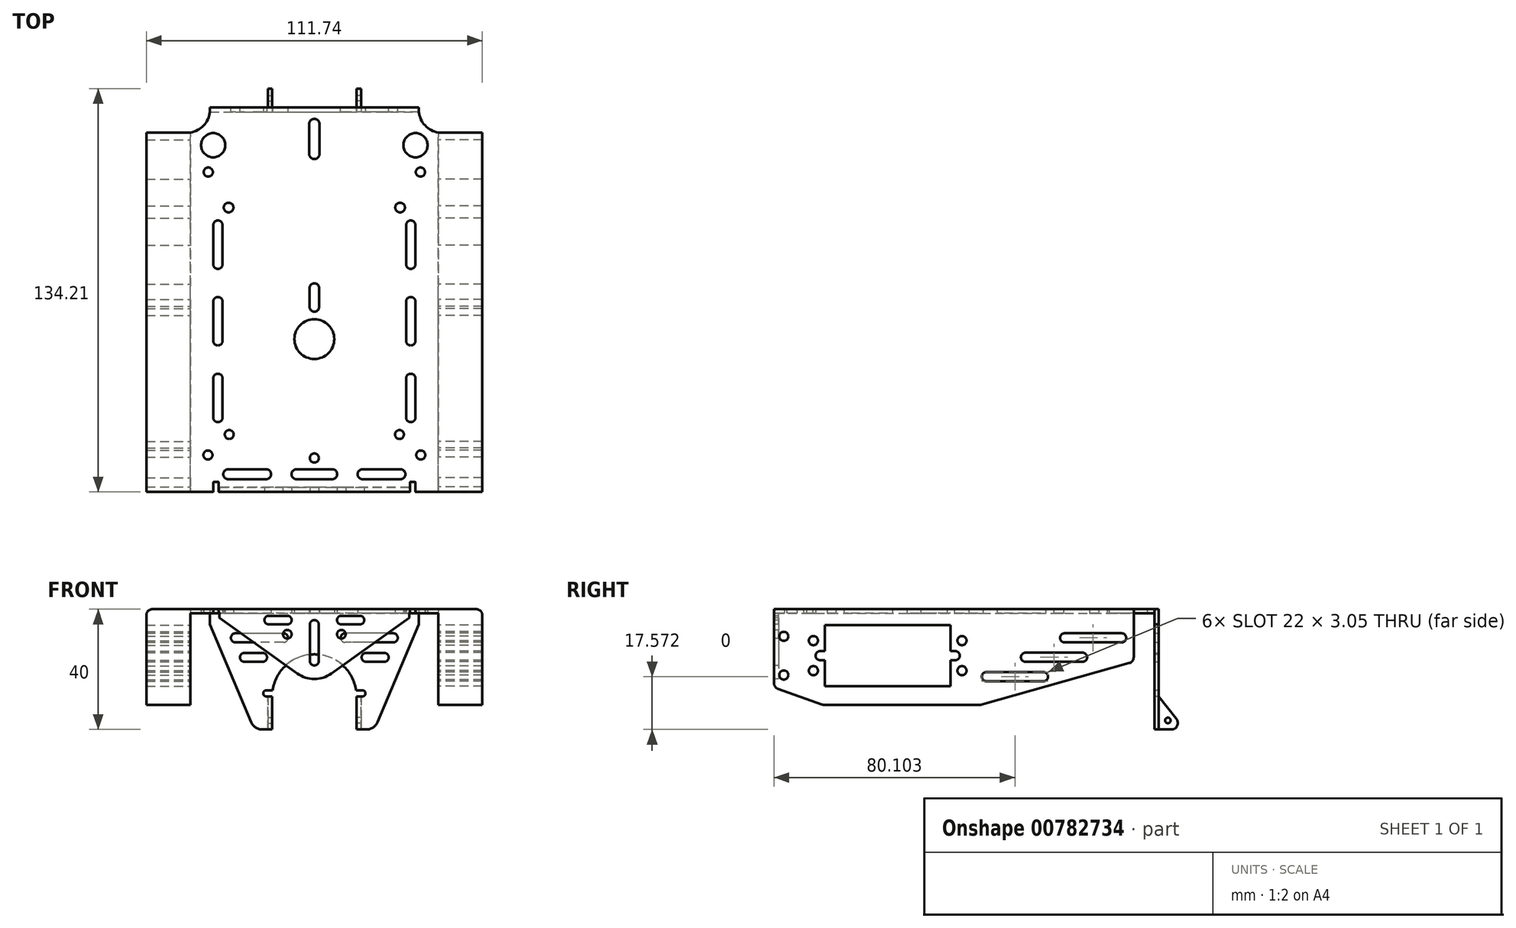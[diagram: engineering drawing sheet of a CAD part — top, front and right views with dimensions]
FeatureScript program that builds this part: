
annotation { "Feature Type Name" : "Feature", "Feature Type Description" : "" }
export const myFeature = defineFeature(function(context is Context, id is Id, definition is map)
    precondition{}
    {
        {
            var Q0;
            Q0=qCreatedBy(makeId("Top.planeOp"),FACE);
            var sketch = newSketch(context, id + "F0", { "sketchPlane" : qUnion([Q0])});
            skLineSegment(sketch, "E0", {"start": v(40.6, 10) * mm, "end": v(40.6, 161.38) * mm});
            skArc(sketch, "E1", {"start": v(40.6, 161.38) * mm, "mid": v(46.2, 164.32) * mm, "end": v(48.85, 170.09) * mm});
            skLineSegment(sketch, "E2", {"start": v(48.85, 170.09) * mm, "end": v(92.83, 170.09) * mm});
            skLineSegment(sketch, "E3", {"start": v(92.83, 170.09) * mm, "end": v(92.83, 10) * mm});
            skLineSegment(sketch, "E4", {"start": v(92.83, 10) * mm, "end": v(52.83, 10) * mm});
            skCircle(sketch, "E5", {"center": v(50.26, 156.03) * mm, "radius": 5.1 * mm});
            skCircle(sketch, "E6", {"center": v(48.18, 144.7) * mm, "radius": 1.93 * mm});
            skCircle(sketch, "E7", {"center": v(56.74, 129.77) * mm, "radius": 2.04 * mm});
            skCircle(sketch, "E8", {"center": v(57.01, 34.19) * mm, "radius": 1.88 * mm});
            skLineSegment(sketch, "E9.left", {"start": v(50.29, 122.36) * mm, "end": v(50.29, 105.92) * mm});
            skLineSegment(sketch, "E9.right", {"start": v(54.22, 122.36) * mm, "end": v(54.22, 105.92) * mm});
            skLineSegment(sketch, "E10.bottom", {"start": v(56.62, 19.58) * mm, "end": v(72.52, 19.58) * mm});
            skLineSegment(sketch, "E10.top", {"start": v(56.62, 15.38) * mm, "end": v(72.52, 15.38) * mm});
            skArc(sketch, "E11", {"start": v(50.29, 105.92) * mm, "mid": v(52.25, 103.95) * mm, "end": v(54.22, 105.92) * mm});
            skArc(sketch, "E12", {"start": v(54.22, 122.36) * mm, "mid": v(52.25, 124.33) * mm, "end": v(50.29, 122.36) * mm});
            skArc(sketch, "E13", {"start": v(56.62, 19.58) * mm, "mid": v(54.52, 17.48) * mm, "end": v(56.62, 15.38) * mm});
            skArc(sketch, "E14", {"start": v(72.52, 15.38) * mm, "mid": v(74.62, 17.48) * mm, "end": v(72.52, 19.58) * mm});
            skLineSegment(sketch, "E15.0.1.0", {"start": v(50.29, 90.1) * mm, "end": v(50.29, 73.66) * mm});
            skArc(sketch, "E15.0.1.1", {"start": v(54.22, 90.1) * mm, "mid": v(52.25, 92.07) * mm, "end": v(50.29, 90.1) * mm});
            skLineSegment(sketch, "E15.0.1.2", {"start": v(54.22, 90.1) * mm, "end": v(54.22, 73.66) * mm});
            skArc(sketch, "E15.0.1.3", {"start": v(50.29, 73.66) * mm, "mid": v(52.25, 71.7) * mm, "end": v(54.22, 73.66) * mm});
            skLineSegment(sketch, "E15.0.2.0", {"start": v(50.29, 57.84) * mm, "end": v(50.29, 41.4) * mm});
            skArc(sketch, "E15.0.2.1", {"start": v(54.22, 57.84) * mm, "mid": v(52.25, 59.8) * mm, "end": v(50.29, 57.84) * mm});
            skLineSegment(sketch, "E15.0.2.2", {"start": v(54.22, 57.84) * mm, "end": v(54.22, 41.4) * mm});
            skArc(sketch, "E15.0.2.3", {"start": v(50.29, 41.4) * mm, "mid": v(52.25, 39.43) * mm, "end": v(54.22, 41.4) * mm});
            skLineSegment(sketch, "E15.direction1", {"start": v(50.29, 105.92) * mm, "end": v(75.69, 105.92) * mm, "construction": true});
            skLineSegment(sketch, "E15.direction2", {"start": v(50.29, 105.92) * mm, "end": v(50.29, 73.66) * mm, "construction": true});
            skCircle(sketch, "E16", {"center": v(48.04, 25.57) * mm, "radius": 1.9 * mm});
            skArc(sketch, "E17", {"start": v(92.83, 82.78) * mm, "mid": v(84.45, 74.4) * mm, "end": v(92.83, 66.02) * mm});
            skArc(sketch, "E18", {"start": v(92.83, 26.24) * mm, "mid": v(90.9, 24.3) * mm, "end": v(92.83, 22.37) * mm});
            skLineSegment(sketch, "E19.left", {"start": v(90.68, 164.98) * mm, "end": v(90.68, 152.35) * mm});
            skArc(sketch, "E20", {"start": v(92.83, 167.14) * mm, "mid": v(91.3, 166.5) * mm, "end": v(90.68, 164.98) * mm});
            skArc(sketch, "E21", {"start": v(90.68, 152.35) * mm, "mid": v(91.3, 150.83) * mm, "end": v(92.83, 150.2) * mm});
            skLineSegment(sketch, "E22.left", {"start": v(90.82, 95.9) * mm, "end": v(90.82, 87.93) * mm});
            skArc(sketch, "E23", {"start": v(92.83, 97.9) * mm, "mid": v(91.4, 97.31) * mm, "end": v(90.82, 95.9) * mm});
            skArc(sketch, "E24", {"start": v(90.82, 87.93) * mm, "mid": v(91.4, 86.5) * mm, "end": v(92.83, 85.92) * mm});
            skLineSegment(sketch, "E25.1.0.0", {"start": v(85.32, 19.58) * mm, "end": v(92.83, 19.58) * mm});
            skArc(sketch, "E25.1.0.1", {"start": v(85.32, 19.58) * mm, "mid": v(83.22, 17.48) * mm, "end": v(85.32, 15.38) * mm});
            skLineSegment(sketch, "E25.1.0.2", {"start": v(85.32, 15.38) * mm, "end": v(92.83, 15.38) * mm});
            skLineSegment(sketch, "E25.direction1", {"start": v(56.62, 15.38) * mm, "end": v(85.32, 15.38) * mm, "construction": true});
            skPoint(sketch, "E26.orphan", {"position": v(101.22, 15.38) * mm});
            skArc(sketch, "E27.MirrorCS", {"start": v(135.38, 105.92) * mm, "mid": v(133.4, 103.95) * mm, "end": v(131.44, 105.92) * mm});
            skArc(sketch, "E28.MirrorCS", {"start": v(131.44, 90.1) * mm, "mid": v(133.4, 92.07) * mm, "end": v(135.38, 90.1) * mm});
            skArc(sketch, "E29.MirrorCS", {"start": v(100.34, 19.58) * mm, "mid": v(102.44, 17.48) * mm, "end": v(100.34, 15.38) * mm});
            skArc(sketch, "E30.MirrorCS", {"start": v(135.38, 41.4) * mm, "mid": v(133.4, 39.43) * mm, "end": v(131.44, 41.4) * mm});
            skArc(sketch, "E31.MirrorCS", {"start": v(113.14, 15.38) * mm, "mid": v(111.04, 17.48) * mm, "end": v(113.14, 19.58) * mm});
            skArc(sketch, "E32.MirrorCS", {"start": v(129.04, 19.58) * mm, "mid": v(131.14, 17.48) * mm, "end": v(129.04, 15.38) * mm});
            skArc(sketch, "E33.MirrorCS", {"start": v(94.84, 87.93) * mm, "mid": v(94.25, 86.5) * mm, "end": v(92.83, 85.92) * mm});
            skArc(sketch, "E34.MirrorCS", {"start": v(135.38, 73.66) * mm, "mid": v(133.4, 71.7) * mm, "end": v(131.44, 73.66) * mm});
            skArc(sketch, "E35.MirrorCS", {"start": v(145.06, 161.38) * mm, "mid": v(139.45, 164.32) * mm, "end": v(136.82, 170.09) * mm});
            skArc(sketch, "E36.MirrorCS", {"start": v(131.44, 57.84) * mm, "mid": v(133.4, 59.8) * mm, "end": v(135.38, 57.84) * mm});
            skArc(sketch, "E37.MirrorCS", {"start": v(131.44, 122.36) * mm, "mid": v(133.4, 124.33) * mm, "end": v(135.38, 122.36) * mm});
            skArc(sketch, "E38.MirrorCS", {"start": v(92.83, 97.9) * mm, "mid": v(94.25, 97.31) * mm, "end": v(94.84, 95.9) * mm});
            skLineSegment(sketch, "E39.MirrorCS", {"start": v(94.99, 164.98) * mm, "end": v(94.99, 152.35) * mm});
            skLineSegment(sketch, "E40.MirrorCS", {"start": v(94.84, 95.9) * mm, "end": v(94.84, 87.93) * mm});
            skLineSegment(sketch, "E41.MirrorCS", {"start": v(100.34, 19.58) * mm, "end": v(92.83, 19.58) * mm});
            skArc(sketch, "E42.MirrorCS", {"start": v(92.83, 167.14) * mm, "mid": v(94.35, 166.5) * mm, "end": v(94.99, 164.98) * mm});
            skArc(sketch, "E43.MirrorCS", {"start": v(94.99, 152.35) * mm, "mid": v(94.35, 150.83) * mm, "end": v(92.83, 150.2) * mm});
            skLineSegment(sketch, "E44.MirrorCS", {"start": v(100.34, 15.38) * mm, "end": v(92.83, 15.38) * mm});
            skArc(sketch, "E45.MirrorCS", {"start": v(92.83, 26.24) * mm, "mid": v(94.77, 24.3) * mm, "end": v(92.83, 22.37) * mm});
            skCircle(sketch, "E46.MirrorC", {"center": v(128.92, 129.77) * mm, "radius": 2.04 * mm});
            skCircle(sketch, "E47.MirrorC", {"center": v(137.62, 25.57) * mm, "radius": 1.9 * mm});
            skCircle(sketch, "E48.MirrorC", {"center": v(137.48, 144.7) * mm, "radius": 1.93 * mm});
            skCircle(sketch, "E49.MirrorC", {"center": v(128.65, 34.19) * mm, "radius": 1.88 * mm});
            skLineSegment(sketch, "E50.MirrorCS", {"start": v(129.04, 15.38) * mm, "end": v(100.34, 15.38) * mm, "construction": true});
            skPoint(sketch, "E51.MirrorP", {"position": v(84.44, 15.38) * mm});
            skCircle(sketch, "E52.MirrorC", {"center": v(135.4, 156.03) * mm, "radius": 5.1 * mm});
            skLineSegment(sketch, "E53.MirrorCS", {"start": v(135.38, 122.36) * mm, "end": v(135.38, 105.92) * mm});
            skLineSegment(sketch, "E54.MirrorCS", {"start": v(135.38, 57.84) * mm, "end": v(135.38, 41.4) * mm});
            skLineSegment(sketch, "E55.MirrorCS", {"start": v(92.83, 10) * mm, "end": v(132.84, 10) * mm});
            skLineSegment(sketch, "E56.MirrorCS", {"start": v(135.38, 105.92) * mm, "end": v(109.98, 105.92) * mm, "construction": true});
            skLineSegment(sketch, "E57.MirrorCS", {"start": v(135.38, 105.92) * mm, "end": v(135.38, 73.66) * mm, "construction": true});
            skLineSegment(sketch, "E58.MirrorCS", {"start": v(135.38, 90.1) * mm, "end": v(135.38, 73.66) * mm});
            skLineSegment(sketch, "E59.MirrorCS", {"start": v(129.04, 19.58) * mm, "end": v(113.14, 19.58) * mm});
            skLineSegment(sketch, "E60.MirrorCS", {"start": v(131.44, 57.84) * mm, "end": v(131.44, 41.4) * mm});
            skLineSegment(sketch, "E61.MirrorCS", {"start": v(129.04, 15.38) * mm, "end": v(113.14, 15.38) * mm});
            skLineSegment(sketch, "E62.MirrorCS", {"start": v(131.44, 122.36) * mm, "end": v(131.44, 105.92) * mm});
            skLineSegment(sketch, "E63.MirrorCS", {"start": v(145.06, 10) * mm, "end": v(145.06, 161.38) * mm});
            skLineSegment(sketch, "E64.MirrorCS", {"start": v(131.44, 90.1) * mm, "end": v(131.44, 73.66) * mm});
            skLineSegment(sketch, "E65.MirrorCS", {"start": v(136.82, 170.09) * mm, "end": v(92.83, 170.09) * mm});
            skArc(sketch, "E66.MirrorCS", {"start": v(92.83, 82.78) * mm, "mid": v(101.21, 74.4) * mm, "end": v(92.83, 66.02) * mm});
            skLineSegment(sketch, "E67", {"start": v(50.36, 10.25) * mm, "end": v(50.36, 14.04) * mm});
            skLineSegment(sketch, "E68", {"start": v(50.62, 14.3) * mm, "end": v(52.32, 14.3) * mm});
            skLineSegment(sketch, "E69", {"start": v(52.57, 14.04) * mm, "end": v(52.57, 10.25) * mm});
            skLineSegment(sketch, "E70.trimOffspring", {"start": v(50.1, 10) * mm, "end": v(40.6, 10) * mm});
            skPoint(sketch, "E71.visualSharp", {"position": v(50.36, 10) * mm});
            skArc(sketch, "E71.filletArc", {"start": v(50.1, 10) * mm, "mid": v(50.29, 10.07) * mm, "end": v(50.36, 10.25) * mm});
            skPoint(sketch, "E72.visualSharp", {"position": v(52.57, 10) * mm});
            skArc(sketch, "E72.filletArc", {"start": v(52.57, 10.25) * mm, "mid": v(52.65, 10.07) * mm, "end": v(52.83, 10) * mm});
            skPoint(sketch, "E73.visualSharp", {"position": v(50.36, 14.3) * mm});
            skArc(sketch, "E73.filletArc", {"start": v(50.62, 14.3) * mm, "mid": v(50.44, 14.22) * mm, "end": v(50.36, 14.04) * mm});
            skPoint(sketch, "E74.visualSharp", {"position": v(52.57, 14.3) * mm});
            skArc(sketch, "E74.filletArc", {"start": v(52.57, 14.04) * mm, "mid": v(52.5, 14.22) * mm, "end": v(52.32, 14.3) * mm});
            skArc(sketch, "E75.MirrorCS", {"start": v(133.09, 10.25) * mm, "mid": v(133.01, 10.07) * mm, "end": v(132.84, 10) * mm});
            skLineSegment(sketch, "E76.MirrorCS", {"start": v(133.09, 14.04) * mm, "end": v(133.09, 10.25) * mm});
            skArc(sketch, "E77.MirrorCS", {"start": v(133.09, 14.04) * mm, "mid": v(133.16, 14.22) * mm, "end": v(133.34, 14.3) * mm});
            skLineSegment(sketch, "E78.MirrorCS", {"start": v(135.3, 10.25) * mm, "end": v(135.3, 14.04) * mm});
            skLineSegment(sketch, "E79.MirrorCS", {"start": v(135.05, 14.3) * mm, "end": v(133.34, 14.3) * mm});
            skArc(sketch, "E80.MirrorCS", {"start": v(135.05, 14.3) * mm, "mid": v(135.23, 14.22) * mm, "end": v(135.3, 14.04) * mm});
            skArc(sketch, "E81.MirrorCS", {"start": v(135.55, 10) * mm, "mid": v(135.37, 10.07) * mm, "end": v(135.3, 10.25) * mm});
            skLineSegment(sketch, "E82.trimOffspring", {"start": v(135.55, 10) * mm, "end": v(145.06, 10) * mm});
            skSolve(sketch);
        }
        {
            var Q0;
            Q0=qSketchRegion(id+"F0",true);
            extrude(context, id + "F1", {"entities" : qUnion([Q0]), "depth" : 1.65 * mm, "offsetDistance" : 25.4 * mm});
        }
        {
            var Q0;
            Q0=makeQuery(id+"F1.opExtrude","SWEPT_BODY",BODY,{"disambiguationData":[OSD([sQuery(id+"F0.wireOp",EDGE,"E0"),sQuery(id+"F0.wireOp",EDGE,"E1"),sQuery(id+"F0.wireOp",EDGE,"E2"),sQuery(id+"F0.wireOp",EDGE,"E4"),sQuery(id+"F0.wireOp",EDGE,"E5"),sQuery(id+"F0.wireOp",EDGE,"E6"),sQuery(id+"F0.wireOp",EDGE,"E7"),sQuery(id+"F0.wireOp",EDGE,"E8"),sQuery(id+"F0.wireOp",EDGE,"E9.left"),sQuery(id+"F0.wireOp",EDGE,"E9.right"),sQuery(id+"F0.wireOp",EDGE,"E10.bottom"),sQuery(id+"F0.wireOp",EDGE,"E10.top"),sQuery(id+"F0.wireOp",EDGE,"E11"),sQuery(id+"F0.wireOp",EDGE,"E12"),sQuery(id+"F0.wireOp",EDGE,"E13"),sQuery(id+"F0.wireOp",EDGE,"E14"),sQuery(id+"F0.wireOp",EDGE,"E15.0.1.0"),sQuery(id+"F0.wireOp",EDGE,"E15.0.1.1"),sQuery(id+"F0.wireOp",EDGE,"E15.0.1.2"),sQuery(id+"F0.wireOp",EDGE,"E15.0.1.3"),sQuery(id+"F0.wireOp",EDGE,"E15.0.2.0"),sQuery(id+"F0.wireOp",EDGE,"E15.0.2.1"),sQuery(id+"F0.wireOp",EDGE,"E15.0.2.2"),sQuery(id+"F0.wireOp",EDGE,"E15.0.2.3"),sQuery(id+"F0.wireOp",EDGE,"E16"),sQuery(id+"F0.wireOp",EDGE,"E17"),sQuery(id+"F0.wireOp",EDGE,"E18"),sQuery(id+"F0.wireOp",EDGE,"E19.left"),sQuery(id+"F0.wireOp",EDGE,"E20"),sQuery(id+"F0.wireOp",EDGE,"E21"),sQuery(id+"F0.wireOp",EDGE,"E22.left"),sQuery(id+"F0.wireOp",EDGE,"E23"),sQuery(id+"F0.wireOp",EDGE,"E24"),sQuery(id+"F0.wireOp",EDGE,"E25.1.0.0"),sQuery(id+"F0.wireOp",EDGE,"E25.1.0.1"),sQuery(id+"F0.wireOp",EDGE,"E25.1.0.2"),sQuery(id+"F0.wireOp",EDGE,"E27.MirrorCS"),sQuery(id+"F0.wireOp",EDGE,"E28.MirrorCS"),sQuery(id+"F0.wireOp",EDGE,"E29.MirrorCS"),sQuery(id+"F0.wireOp",EDGE,"E30.MirrorCS"),sQuery(id+"F0.wireOp",EDGE,"E31.MirrorCS"),sQuery(id+"F0.wireOp",EDGE,"E32.MirrorCS"),sQuery(id+"F0.wireOp",EDGE,"E33.MirrorCS"),sQuery(id+"F0.wireOp",EDGE,"E34.MirrorCS"),sQuery(id+"F0.wireOp",EDGE,"E35.MirrorCS"),sQuery(id+"F0.wireOp",EDGE,"E36.MirrorCS"),sQuery(id+"F0.wireOp",EDGE,"E37.MirrorCS"),sQuery(id+"F0.wireOp",EDGE,"E38.MirrorCS"),sQuery(id+"F0.wireOp",EDGE,"E39.MirrorCS"),sQuery(id+"F0.wireOp",EDGE,"E40.MirrorCS"),sQuery(id+"F0.wireOp",EDGE,"E41.MirrorCS"),sQuery(id+"F0.wireOp",EDGE,"E42.MirrorCS"),sQuery(id+"F0.wireOp",EDGE,"E43.MirrorCS"),sQuery(id+"F0.wireOp",EDGE,"E44.MirrorCS"),sQuery(id+"F0.wireOp",EDGE,"E45.MirrorCS"),sQuery(id+"F0.wireOp",EDGE,"E46.MirrorC"),sQuery(id+"F0.wireOp",EDGE,"E47.MirrorC"),sQuery(id+"F0.wireOp",EDGE,"E48.MirrorC"),sQuery(id+"F0.wireOp",EDGE,"E49.MirrorC"),sQuery(id+"F0.wireOp",EDGE,"E52.MirrorC"),sQuery(id+"F0.wireOp",EDGE,"E53.MirrorCS"),sQuery(id+"F0.wireOp",EDGE,"E54.MirrorCS"),sQuery(id+"F0.wireOp",EDGE,"E55.MirrorCS"),sQuery(id+"F0.wireOp",EDGE,"E58.MirrorCS"),sQuery(id+"F0.wireOp",EDGE,"E59.MirrorCS"),sQuery(id+"F0.wireOp",EDGE,"E60.MirrorCS"),sQuery(id+"F0.wireOp",EDGE,"E61.MirrorCS"),sQuery(id+"F0.wireOp",EDGE,"E62.MirrorCS"),sQuery(id+"F0.wireOp",EDGE,"E63.MirrorCS"),sQuery(id+"F0.wireOp",EDGE,"E64.MirrorCS"),sQuery(id+"F0.wireOp",EDGE,"E65.MirrorCS"),sQuery(id+"F0.wireOp",EDGE,"E66.MirrorCS")])]});
            var Q1;
            Q1=qCreatedBy(makeId("Origin.pointOp"),VERTEX);
            transform(context, id + "F2", {"entities" : qUnion([Q0]), "transformType" : TransformType.SCALE_UNIFORMLY, "scale" : .83151, "scalePoint" : qUnion([Q1]), "makeCopy" : false});
        }
        {
            var Q0;
            Q0=makeQuery(id+"F1.opExtrude","SWEPT_FACE",FACE,{"disambiguationData":[OSD([sQuery(id+"F0.wireOp",EDGE,"E4")])]});
            var sketch = newSketch(context, id + "F3", { "sketchPlane" : qUnion([Q0])});
            skLineSegment(sketch, "E83", {"start": v(43.93, -1.68) * mm, "end": v(43.93, 0) * mm});
            skLineSegment(sketch, "E84", {"start": v(110.45, 0) * mm, "end": v(110.45, -1.68) * mm});
            skLineSegment(sketch, "E85", {"start": v(43.93, 0) * mm, "end": v(110.45, 0) * mm});
            skLineSegment(sketch, "E86", {"start": v(43.93, -1.68) * mm, "end": v(71.3, -21.2) * mm});
            skLineSegment(sketch, "E87", {"start": v(83.09, -21.2) * mm, "end": v(110.45, -1.68) * mm});
            skLineSegment(sketch, "E88", {"start": v(77.19, -25.4) * mm, "end": v(77.19, 0) * mm, "construction": true});
            skPoint(sketch, "E89.visualSharp", {"position": v(77.19, -25.4) * mm});
            skArc(sketch, "E89.filletArc", {"start": v(71.3, -21.2) * mm, "mid": v(77.19, -23.08) * mm, "end": v(83.09, -21.2) * mm});
            skPoint(sketch, "E90", {"position": v(77.19, -23.08) * mm});
            skArc(sketch, "E91", {"start": v(78.74, -3.99) * mm, "mid": v(77.19, -2.44) * mm, "end": v(75.64, -3.99) * mm});
            skLineSegment(sketch, "E92", {"start": v(75.64, -3.99) * mm, "end": v(75.64, -10.37) * mm});
            skLineSegment(sketch, "E93", {"start": v(78.74, -3.99) * mm, "end": v(78.74, -10.37) * mm});
            skPoint(sketch, "E94", {"position": v(77.19, -2.44) * mm});
            skLineSegment(sketch, "E95", {"start": v(75.64, -10.37) * mm, "end": v(78.74, -10.37) * mm, "construction": true});
            skLineSegment(sketch, "E96.MirrorCS", {"start": v(78.74, -16.76) * mm, "end": v(78.74, -10.37) * mm});
            skLineSegment(sketch, "E97.MirrorCS", {"start": v(75.64, -16.76) * mm, "end": v(75.64, -10.37) * mm});
            skArc(sketch, "E98.MirrorCS", {"start": v(78.74, -16.76) * mm, "mid": v(77.19, -18.31) * mm, "end": v(75.64, -16.76) * mm});
            skArc(sketch, "E99", {"start": v(86.65, -0.91) * mm, "mid": v(85.13, -2.44) * mm, "end": v(86.65, -3.96) * mm});
            skLineSegment(sketch, "E100", {"start": v(86.65, -0.91) * mm, "end": v(89.89, -0.91) * mm});
            skLineSegment(sketch, "E101", {"start": v(86.65, -3.96) * mm, "end": v(89.89, -3.96) * mm});
            skLineSegment(sketch, "E102", {"start": v(86.65, -2.44) * mm, "end": v(85.13, -2.44) * mm, "construction": true});
            skPoint(sketch, "E103", {"position": v(85.13, -2.44) * mm});
            skLineSegment(sketch, "E104", {"start": v(89.89, -0.91) * mm, "end": v(89.89, -3.96) * mm, "construction": true});
            skLineSegment(sketch, "E105.MirrorCS", {"start": v(93.13, -0.91) * mm, "end": v(89.89, -0.91) * mm});
            skLineSegment(sketch, "E106.MirrorCS", {"start": v(93.13, -3.96) * mm, "end": v(89.89, -3.96) * mm});
            skArc(sketch, "E107.MirrorCS", {"start": v(93.13, -0.91) * mm, "mid": v(94.65, -2.44) * mm, "end": v(93.13, -3.96) * mm});
            skLineSegment(sketch, "E108.MirrorCS", {"start": v(67.73, -2.44) * mm, "end": v(69.25, -2.44) * mm, "construction": true});
            skLineSegment(sketch, "E109.MirrorCS", {"start": v(64.49, -0.91) * mm, "end": v(64.49, -3.96) * mm, "construction": true});
            skLineSegment(sketch, "E110.MirrorCS", {"start": v(67.73, -3.96) * mm, "end": v(64.49, -3.96) * mm});
            skLineSegment(sketch, "E111.MirrorCS", {"start": v(67.73, -0.91) * mm, "end": v(64.49, -0.91) * mm});
            skLineSegment(sketch, "E112.MirrorCS", {"start": v(61.25, -3.96) * mm, "end": v(64.49, -3.96) * mm});
            skArc(sketch, "E113.MirrorCS", {"start": v(67.73, -0.91) * mm, "mid": v(69.25, -2.44) * mm, "end": v(67.73, -3.96) * mm});
            skLineSegment(sketch, "E114.MirrorCS", {"start": v(61.25, -0.91) * mm, "end": v(64.49, -0.91) * mm});
            skArc(sketch, "E115.MirrorCS", {"start": v(61.25, -0.91) * mm, "mid": v(59.73, -2.44) * mm, "end": v(61.25, -3.96) * mm});
            skPoint(sketch, "E116.MirrorP", {"position": v(69.25, -2.44) * mm});
            skCircle(sketch, "E117", {"center": v(86.65, -7.4) * mm, "radius": 1.52 * mm});
            skCircle(sketch, "E118.MirrorC", {"center": v(67.73, -7.4) * mm, "radius": 1.52 * mm});
            skSolve(sketch);
        }
        {
            var Q0;
            Q0=qSketchRegion(id+"F3",true);
            extrude(context, id + "F4", {"entities" : qUnion([Q0]), "operationType" : NewBodyOperationType.ADD, "oppositeDirection" : true, "depth" : 1.65 * mm, "offsetDistance" : 25.4 * mm});
        }
        {
            var Q0;
            Q0=makeQuery(id+"F1.opExtrude","CAP_EDGE",EDGE,{"disambiguationData":[OSD([sQuery(id+"F0.wireOp",EDGE,"E4"),sQuery(id+"F0.wireOp",EDGE,"E55.MirrorCS")])],"isStart":false});
            fillet(context, id + "F5", {"entities" : qUnion([Q0]), "radius" : 1.27 * mm, "allowEdgeOverflow" : false});
        }
        {
            var Q0;
            Q0=makeQuery(id+"F1.opExtrude","SWEPT_BODY",BODY,{"disambiguationData":[OSD([sQuery(id+"F0.wireOp",EDGE,"E0"),sQuery(id+"F0.wireOp",EDGE,"E1"),sQuery(id+"F0.wireOp",EDGE,"E2"),sQuery(id+"F0.wireOp",EDGE,"E4"),sQuery(id+"F0.wireOp",EDGE,"E5"),sQuery(id+"F0.wireOp",EDGE,"E6"),sQuery(id+"F0.wireOp",EDGE,"E7"),sQuery(id+"F0.wireOp",EDGE,"E8"),sQuery(id+"F0.wireOp",EDGE,"E9.left"),sQuery(id+"F0.wireOp",EDGE,"E9.right"),sQuery(id+"F0.wireOp",EDGE,"E10.bottom"),sQuery(id+"F0.wireOp",EDGE,"E10.top"),sQuery(id+"F0.wireOp",EDGE,"E11"),sQuery(id+"F0.wireOp",EDGE,"E12"),sQuery(id+"F0.wireOp",EDGE,"E13"),sQuery(id+"F0.wireOp",EDGE,"E14"),sQuery(id+"F0.wireOp",EDGE,"E15.0.1.0"),sQuery(id+"F0.wireOp",EDGE,"E15.0.1.1"),sQuery(id+"F0.wireOp",EDGE,"E15.0.1.2"),sQuery(id+"F0.wireOp",EDGE,"E15.0.1.3"),sQuery(id+"F0.wireOp",EDGE,"E15.0.2.0"),sQuery(id+"F0.wireOp",EDGE,"E15.0.2.1"),sQuery(id+"F0.wireOp",EDGE,"E15.0.2.2"),sQuery(id+"F0.wireOp",EDGE,"E15.0.2.3"),sQuery(id+"F0.wireOp",EDGE,"E16"),sQuery(id+"F0.wireOp",EDGE,"E17"),sQuery(id+"F0.wireOp",EDGE,"E18"),sQuery(id+"F0.wireOp",EDGE,"E19.left"),sQuery(id+"F0.wireOp",EDGE,"E20"),sQuery(id+"F0.wireOp",EDGE,"E21"),sQuery(id+"F0.wireOp",EDGE,"E22.left"),sQuery(id+"F0.wireOp",EDGE,"E23"),sQuery(id+"F0.wireOp",EDGE,"E24"),sQuery(id+"F0.wireOp",EDGE,"E25.1.0.0"),sQuery(id+"F0.wireOp",EDGE,"E25.1.0.1"),sQuery(id+"F0.wireOp",EDGE,"E25.1.0.2"),sQuery(id+"F0.wireOp",EDGE,"E27.MirrorCS"),sQuery(id+"F0.wireOp",EDGE,"E28.MirrorCS"),sQuery(id+"F0.wireOp",EDGE,"E29.MirrorCS"),sQuery(id+"F0.wireOp",EDGE,"E30.MirrorCS"),sQuery(id+"F0.wireOp",EDGE,"E31.MirrorCS"),sQuery(id+"F0.wireOp",EDGE,"E32.MirrorCS"),sQuery(id+"F0.wireOp",EDGE,"E33.MirrorCS"),sQuery(id+"F0.wireOp",EDGE,"E34.MirrorCS"),sQuery(id+"F0.wireOp",EDGE,"E35.MirrorCS"),sQuery(id+"F0.wireOp",EDGE,"E36.MirrorCS"),sQuery(id+"F0.wireOp",EDGE,"E37.MirrorCS"),sQuery(id+"F0.wireOp",EDGE,"E38.MirrorCS"),sQuery(id+"F0.wireOp",EDGE,"E39.MirrorCS"),sQuery(id+"F0.wireOp",EDGE,"E40.MirrorCS"),sQuery(id+"F0.wireOp",EDGE,"E41.MirrorCS"),sQuery(id+"F0.wireOp",EDGE,"E42.MirrorCS"),sQuery(id+"F0.wireOp",EDGE,"E43.MirrorCS"),sQuery(id+"F0.wireOp",EDGE,"E44.MirrorCS"),sQuery(id+"F0.wireOp",EDGE,"E45.MirrorCS"),sQuery(id+"F0.wireOp",EDGE,"E46.MirrorC"),sQuery(id+"F0.wireOp",EDGE,"E47.MirrorC"),sQuery(id+"F0.wireOp",EDGE,"E48.MirrorC"),sQuery(id+"F0.wireOp",EDGE,"E49.MirrorC"),sQuery(id+"F0.wireOp",EDGE,"E52.MirrorC"),sQuery(id+"F0.wireOp",EDGE,"E53.MirrorCS"),sQuery(id+"F0.wireOp",EDGE,"E54.MirrorCS"),sQuery(id+"F0.wireOp",EDGE,"E55.MirrorCS"),sQuery(id+"F0.wireOp",EDGE,"E58.MirrorCS"),sQuery(id+"F0.wireOp",EDGE,"E59.MirrorCS"),sQuery(id+"F0.wireOp",EDGE,"E60.MirrorCS"),sQuery(id+"F0.wireOp",EDGE,"E61.MirrorCS"),sQuery(id+"F0.wireOp",EDGE,"E62.MirrorCS"),sQuery(id+"F0.wireOp",EDGE,"E63.MirrorCS"),sQuery(id+"F0.wireOp",EDGE,"E64.MirrorCS"),sQuery(id+"F0.wireOp",EDGE,"E65.MirrorCS"),sQuery(id+"F0.wireOp",EDGE,"E66.MirrorCS"),sQuery(id+"F0.wireOp",EDGE,"E67"),sQuery(id+"F0.wireOp",EDGE,"E68"),sQuery(id+"F0.wireOp",EDGE,"E69"),sQuery(id+"F0.wireOp",EDGE,"E70.trimOffspring"),sQuery(id+"F0.wireOp",EDGE,"E71.filletArc"),sQuery(id+"F0.wireOp",EDGE,"E72.filletArc"),sQuery(id+"F0.wireOp",EDGE,"E73.filletArc"),sQuery(id+"F0.wireOp",EDGE,"E74.filletArc"),sQuery(id+"F0.wireOp",EDGE,"E75.MirrorCS"),sQuery(id+"F0.wireOp",EDGE,"E76.MirrorCS"),sQuery(id+"F0.wireOp",EDGE,"E77.MirrorCS"),sQuery(id+"F0.wireOp",EDGE,"E78.MirrorCS"),sQuery(id+"F0.wireOp",EDGE,"E79.MirrorCS"),sQuery(id+"F0.wireOp",EDGE,"E80.MirrorCS"),sQuery(id+"F0.wireOp",EDGE,"E81.MirrorCS"),sQuery(id+"F0.wireOp",EDGE,"E82.trimOffspring")])]});
            var Q1;
            Q1=qCreatedBy(makeId("Origin.pointOp"),VERTEX);
            transform(context, id + "F6", {"entities" : qUnion([Q0]), "transformType" : TransformType.SCALE_UNIFORMLY, "scale" : .95, "scalePoint" : qUnion([Q1]), "makeCopy" : false});
        }
        {
            var Q0;
            Q0=makeQuery(id+"F1.opExtrude","SWEPT_FACE",FACE,{"disambiguationData":[OSD([sQuery(id+"F0.wireOp",EDGE,"E0")])]});
            var sketch = newSketch(context, id + "F7", { "sketchPlane" : qUnion([Q0])});
            skLineSegment(sketch, "E119", {"start": v(-7.9, 1.3) * mm, "end": v(-7.9, -23.29) * mm});
            skLineSegment(sketch, "E120", {"start": v(-9.22, -25.17) * mm, "end": v(-23.83, -30.38) * mm});
            skLineSegment(sketch, "E121", {"start": v(-24.5, -30.5) * mm, "end": v(-76.4, -30.5) * mm});
            skLineSegment(sketch, "E122", {"start": v(-76.94, -30.42) * mm, "end": v(-126.02, -16.6) * mm});
            skLineSegment(sketch, "E123", {"start": v(-127.48, -14.68) * mm, "end": v(-127.48, 1.3) * mm});
            skPoint(sketch, "E124.visualSharp", {"position": v(-127.48, -16.2) * mm});
            skArc(sketch, "E124.filletArc", {"start": v(-127.48, -14.68) * mm, "mid": v(-127.07, -15.89) * mm, "end": v(-126.02, -16.6) * mm});
            skPoint(sketch, "E125.visualSharp", {"position": v(-76.68, -30.5) * mm});
            skArc(sketch, "E125.filletArc", {"start": v(-76.94, -30.42) * mm, "mid": v(-76.67, -30.48) * mm, "end": v(-76.4, -30.5) * mm});
            skPoint(sketch, "E126.visualSharp", {"position": v(-24.15, -30.5) * mm});
            skArc(sketch, "E126.filletArc", {"start": v(-24.5, -30.5) * mm, "mid": v(-24.16, -30.47) * mm, "end": v(-23.83, -30.38) * mm});
            skPoint(sketch, "E127.visualSharp", {"position": v(-7.9, -24.7) * mm});
            skArc(sketch, "E127.filletArc", {"start": v(-9.22, -25.17) * mm, "mid": v(-8.26, -24.44) * mm, "end": v(-7.9, -23.29) * mm});
            skLineSegment(sketch, "E128", {"start": v(-127.48, 1.3) * mm, "end": v(-7.9, 1.3) * mm});
            skLineSegment(sketch, "E129.bottom", {"start": v(-66.64, -4.02) * mm, "end": v(-24.74, -4.02) * mm});
            skLineSegment(sketch, "E129.top", {"start": v(-66.64, -24.27) * mm, "end": v(-24.74, -24.27) * mm});
            skLineSegment(sketch, "E129.left", {"start": v(-66.64, -4.02) * mm, "end": v(-66.64, -12.64) * mm});
            skLineSegment(sketch, "E129.right", {"start": v(-24.74, -4.02) * mm, "end": v(-24.74, -12.64) * mm});
            skLineSegment(sketch, "E130", {"start": v(-45.7, -4.02) * mm, "end": v(-45.7, -24.27) * mm, "construction": true});
            skArc(sketch, "E131", {"start": v(-68.14, -12.64) * mm, "mid": v(-69.64, -14.14) * mm, "end": v(-68.14, -15.64) * mm});
            skPoint(sketch, "E131.centerSnap0", {"position": v(-66.64, -14.14) * mm});
            skLineSegment(sketch, "E132", {"start": v(-68.14, -12.64) * mm, "end": v(-66.64, -12.64) * mm});
            skLineSegment(sketch, "E133", {"start": v(-68.14, -15.64) * mm, "end": v(-66.64, -15.64) * mm});
            skLineSegment(sketch, "E134.trimOffspring", {"start": v(-66.64, -15.64) * mm, "end": v(-66.64, -24.27) * mm});
            skArc(sketch, "E135.MirrorCS", {"start": v(-23.24, -12.64) * mm, "mid": v(-21.74, -14.14) * mm, "end": v(-23.24, -15.64) * mm});
            skPoint(sketch, "E136.MirrorP", {"position": v(-24.74, -14.14) * mm});
            skLineSegment(sketch, "E137.MirrorCS", {"start": v(-23.24, -15.64) * mm, "end": v(-24.74, -15.64) * mm});
            skLineSegment(sketch, "E138.MirrorCS", {"start": v(-23.24, -12.64) * mm, "end": v(-24.74, -12.64) * mm});
            skLineSegment(sketch, "E139.trimOffspring", {"start": v(-24.74, -15.64) * mm, "end": v(-24.74, -24.27) * mm});
            skLineSegment(sketch, "E140", {"start": v(-68.14, -14.14) * mm, "end": v(-23.24, -14.14) * mm, "construction": true});
            skCircle(sketch, "E141", {"center": v(-70.4, -9.14) * mm, "radius": 1.52 * mm});
            skCircle(sketch, "E142.0.1.0", {"center": v(-70.4, -19.14) * mm, "radius": 1.52 * mm});
            skCircle(sketch, "E142.1.0.0", {"center": v(-21, -9.14) * mm, "radius": 1.52 * mm});
            skCircle(sketch, "E142.1.1.0", {"center": v(-21, -19.14) * mm, "radius": 1.52 * mm});
            skLineSegment(sketch, "E142.direction1", {"start": v(-70.4, -9.14) * mm, "end": v(-21, -9.14) * mm, "construction": true});
            skLineSegment(sketch, "E142.direction2", {"start": v(-70.4, -9.14) * mm, "end": v(-70.4, -19.14) * mm, "construction": true});
            skCircle(sketch, "E143", {"center": v(-11.15, -7.72) * mm, "radius": 1.52 * mm});
            skCircle(sketch, "E144", {"center": v(-11.15, -20.57) * mm, "radius": 1.52 * mm});
            skLineSegment(sketch, "E145", {"start": v(-11.15, -7.72) * mm, "end": v(-11.15, -20.57) * mm, "construction": true});
            skPoint(sketch, "E146", {"position": v(-11.15, -14.14) * mm});
            skArc(sketch, "E147", {"start": v(-123.48, -6.7) * mm, "mid": v(-125, -8.22) * mm, "end": v(-123.48, -9.74) * mm});
            skLineSegment(sketch, "E148", {"start": v(-123.48, -6.7) * mm, "end": v(-114, -6.7) * mm});
            skLineSegment(sketch, "E149", {"start": v(-123.48, -9.74) * mm, "end": v(-114, -9.74) * mm});
            skLineSegment(sketch, "E150", {"start": v(-114, -9.74) * mm, "end": v(-114, -6.7) * mm, "construction": true});
            skLineSegment(sketch, "E151.MirrorCS", {"start": v(-104.53, -6.7) * mm, "end": v(-114, -6.7) * mm});
            skLineSegment(sketch, "E152.MirrorCS", {"start": v(-104.53, -9.74) * mm, "end": v(-114, -9.74) * mm});
            skArc(sketch, "E153.MirrorCS", {"start": v(-104.53, -6.7) * mm, "mid": v(-103, -8.22) * mm, "end": v(-104.53, -9.74) * mm});
            skLineSegment(sketch, "E154.direction1", {"start": v(-123.48, -9.74) * mm, "end": v(-117.53, -9.74) * mm, "construction": true});
            skLineSegment(sketch, "E154.direction2", {"start": v(-123.48, -9.74) * mm, "end": v(-123.48, -16.2) * mm, "construction": true});
            skPoint(sketch, "E155", {"position": v(-110.48, -14.67) * mm});
            skArc(sketch, "E156", {"start": v(-110.48, -13.15) * mm, "mid": v(-112, -14.67) * mm, "end": v(-110.48, -16.2) * mm});
            skLineSegment(sketch, "E157", {"start": v(-110.48, -13.15) * mm, "end": v(-101, -13.15) * mm});
            skLineSegment(sketch, "E158", {"start": v(-110.48, -16.2) * mm, "end": v(-101, -16.2) * mm});
            skLineSegment(sketch, "E159", {"start": v(-101, -16.2) * mm, "end": v(-101, -13.15) * mm, "construction": true});
            skLineSegment(sketch, "E160.MirrorCS", {"start": v(-91.53, -13.15) * mm, "end": v(-101, -13.15) * mm});
            skLineSegment(sketch, "E161.MirrorCS", {"start": v(-91.53, -16.2) * mm, "end": v(-101, -16.2) * mm});
            skArc(sketch, "E162.MirrorCS", {"start": v(-91.53, -13.15) * mm, "mid": v(-90, -14.67) * mm, "end": v(-91.53, -16.2) * mm});
            skLineSegment(sketch, "E163.direction1", {"start": v(-110.48, -16.2) * mm, "end": v(-104.53, -16.2) * mm, "construction": true});
            skPoint(sketch, "E164", {"position": v(-97.48, -21.12) * mm});
            skArc(sketch, "E165", {"start": v(-97.48, -19.6) * mm, "mid": v(-99, -21.12) * mm, "end": v(-97.48, -22.65) * mm});
            skLineSegment(sketch, "E166", {"start": v(-97.48, -19.6) * mm, "end": v(-88, -19.6) * mm});
            skLineSegment(sketch, "E167", {"start": v(-97.48, -22.65) * mm, "end": v(-88, -22.65) * mm});
            skLineSegment(sketch, "E168", {"start": v(-88, -22.65) * mm, "end": v(-88, -19.6) * mm, "construction": true});
            skLineSegment(sketch, "E169.MirrorCS", {"start": v(-78.53, -19.6) * mm, "end": v(-88, -19.6) * mm});
            skLineSegment(sketch, "E170.MirrorCS", {"start": v(-78.53, -22.65) * mm, "end": v(-88, -22.65) * mm});
            skArc(sketch, "E171.MirrorCS", {"start": v(-78.53, -19.6) * mm, "mid": v(-77, -21.12) * mm, "end": v(-78.53, -22.65) * mm});
            skSolve(sketch);
        }
        {
            var Q0;
            Q0=qSketchRegion(id+"F7",true);
            extrude(context, id + "F8", {"entities" : qUnion([Q0]), "operationType" : NewBodyOperationType.ADD, "depth" : (.575 * 25.4) * mm, "offsetDistance" : 25 * mm});
        }
        {
            var Q0;
            Q0=makeQuery(id+"F1.opExtrude","CAP_EDGE",EDGE,{"disambiguationData":[OSD([sQuery(id+"F0.wireOp",EDGE,"E24"),sQuery(id+"F0.wireOp",EDGE,"E33.MirrorCS")])],"isStart":false});
            cPoint(context, id + "F9", {"entities" : qUnion([Q0]), "parameter" : 0.5});
        }
        {
            var Q0;
            Q0=makeQuery(id+"F1.opExtrude","SWEPT_BODY",BODY,{"disambiguationData":[OSD([sQuery(id+"F0.wireOp",EDGE,"E0"),sQuery(id+"F0.wireOp",EDGE,"E1"),sQuery(id+"F0.wireOp",EDGE,"E2"),sQuery(id+"F0.wireOp",EDGE,"E4"),sQuery(id+"F0.wireOp",EDGE,"E5"),sQuery(id+"F0.wireOp",EDGE,"E6"),sQuery(id+"F0.wireOp",EDGE,"E7"),sQuery(id+"F0.wireOp",EDGE,"E8"),sQuery(id+"F0.wireOp",EDGE,"E9.left"),sQuery(id+"F0.wireOp",EDGE,"E9.right"),sQuery(id+"F0.wireOp",EDGE,"E10.bottom"),sQuery(id+"F0.wireOp",EDGE,"E10.top"),sQuery(id+"F0.wireOp",EDGE,"E11"),sQuery(id+"F0.wireOp",EDGE,"E12"),sQuery(id+"F0.wireOp",EDGE,"E13"),sQuery(id+"F0.wireOp",EDGE,"E14"),sQuery(id+"F0.wireOp",EDGE,"E15.0.1.0"),sQuery(id+"F0.wireOp",EDGE,"E15.0.1.1"),sQuery(id+"F0.wireOp",EDGE,"E15.0.1.2"),sQuery(id+"F0.wireOp",EDGE,"E15.0.1.3"),sQuery(id+"F0.wireOp",EDGE,"E15.0.2.0"),sQuery(id+"F0.wireOp",EDGE,"E15.0.2.1"),sQuery(id+"F0.wireOp",EDGE,"E15.0.2.2"),sQuery(id+"F0.wireOp",EDGE,"E15.0.2.3"),sQuery(id+"F0.wireOp",EDGE,"E16"),sQuery(id+"F0.wireOp",EDGE,"E17"),sQuery(id+"F0.wireOp",EDGE,"E18"),sQuery(id+"F0.wireOp",EDGE,"E19.left"),sQuery(id+"F0.wireOp",EDGE,"E20"),sQuery(id+"F0.wireOp",EDGE,"E21"),sQuery(id+"F0.wireOp",EDGE,"E22.left"),sQuery(id+"F0.wireOp",EDGE,"E23"),sQuery(id+"F0.wireOp",EDGE,"E24"),sQuery(id+"F0.wireOp",EDGE,"E25.1.0.0"),sQuery(id+"F0.wireOp",EDGE,"E25.1.0.1"),sQuery(id+"F0.wireOp",EDGE,"E25.1.0.2"),sQuery(id+"F0.wireOp",EDGE,"E27.MirrorCS"),sQuery(id+"F0.wireOp",EDGE,"E28.MirrorCS"),sQuery(id+"F0.wireOp",EDGE,"E29.MirrorCS"),sQuery(id+"F0.wireOp",EDGE,"E30.MirrorCS"),sQuery(id+"F0.wireOp",EDGE,"E31.MirrorCS"),sQuery(id+"F0.wireOp",EDGE,"E32.MirrorCS"),sQuery(id+"F0.wireOp",EDGE,"E33.MirrorCS"),sQuery(id+"F0.wireOp",EDGE,"E34.MirrorCS"),sQuery(id+"F0.wireOp",EDGE,"E35.MirrorCS"),sQuery(id+"F0.wireOp",EDGE,"E36.MirrorCS"),sQuery(id+"F0.wireOp",EDGE,"E37.MirrorCS"),sQuery(id+"F0.wireOp",EDGE,"E38.MirrorCS"),sQuery(id+"F0.wireOp",EDGE,"E39.MirrorCS"),sQuery(id+"F0.wireOp",EDGE,"E40.MirrorCS"),sQuery(id+"F0.wireOp",EDGE,"E41.MirrorCS"),sQuery(id+"F0.wireOp",EDGE,"E42.MirrorCS"),sQuery(id+"F0.wireOp",EDGE,"E43.MirrorCS"),sQuery(id+"F0.wireOp",EDGE,"E44.MirrorCS"),sQuery(id+"F0.wireOp",EDGE,"E45.MirrorCS"),sQuery(id+"F0.wireOp",EDGE,"E46.MirrorC"),sQuery(id+"F0.wireOp",EDGE,"E47.MirrorC"),sQuery(id+"F0.wireOp",EDGE,"E48.MirrorC"),sQuery(id+"F0.wireOp",EDGE,"E49.MirrorC"),sQuery(id+"F0.wireOp",EDGE,"E52.MirrorC"),sQuery(id+"F0.wireOp",EDGE,"E53.MirrorCS"),sQuery(id+"F0.wireOp",EDGE,"E54.MirrorCS"),sQuery(id+"F0.wireOp",EDGE,"E55.MirrorCS"),sQuery(id+"F0.wireOp",EDGE,"E58.MirrorCS"),sQuery(id+"F0.wireOp",EDGE,"E59.MirrorCS"),sQuery(id+"F0.wireOp",EDGE,"E60.MirrorCS"),sQuery(id+"F0.wireOp",EDGE,"E61.MirrorCS"),sQuery(id+"F0.wireOp",EDGE,"E62.MirrorCS"),sQuery(id+"F0.wireOp",EDGE,"E63.MirrorCS"),sQuery(id+"F0.wireOp",EDGE,"E64.MirrorCS"),sQuery(id+"F0.wireOp",EDGE,"E65.MirrorCS"),sQuery(id+"F0.wireOp",EDGE,"E66.MirrorCS"),sQuery(id+"F0.wireOp",EDGE,"E67"),sQuery(id+"F0.wireOp",EDGE,"E68"),sQuery(id+"F0.wireOp",EDGE,"E69"),sQuery(id+"F0.wireOp",EDGE,"E70.trimOffspring"),sQuery(id+"F0.wireOp",EDGE,"E71.filletArc"),sQuery(id+"F0.wireOp",EDGE,"E72.filletArc"),sQuery(id+"F0.wireOp",EDGE,"E73.filletArc"),sQuery(id+"F0.wireOp",EDGE,"E74.filletArc"),sQuery(id+"F0.wireOp",EDGE,"E75.MirrorCS"),sQuery(id+"F0.wireOp",EDGE,"E76.MirrorCS"),sQuery(id+"F0.wireOp",EDGE,"E77.MirrorCS"),sQuery(id+"F0.wireOp",EDGE,"E78.MirrorCS"),sQuery(id+"F0.wireOp",EDGE,"E79.MirrorCS"),sQuery(id+"F0.wireOp",EDGE,"E80.MirrorCS"),sQuery(id+"F0.wireOp",EDGE,"E81.MirrorCS"),sQuery(id+"F0.wireOp",EDGE,"E82.trimOffspring")])]});
            var Q1;
            Q1=qCreatedBy(id+"F9",VERTEX);
            var Q2;
            Q2=qCreatedBy(makeId("Origin.pointOp"),VERTEX);
            transform(context, id + "F10", {"entities" : qUnion([Q0]), "transformType" : TransformType.TRANSLATION_ENTITY, "oppositeDirectionEntity" : false, "transformLine" : qUnion([Q1, Q2]), "makeCopy" : false});
        }
        {
            var Q0;
            Q0=makeQuery(id+"F1.opExtrude","SWEPT_BODY",BODY,{"disambiguationData":[OSD([sQuery(id+"F0.wireOp",EDGE,"E0"),sQuery(id+"F0.wireOp",EDGE,"E1"),sQuery(id+"F0.wireOp",EDGE,"E2"),sQuery(id+"F0.wireOp",EDGE,"E4"),sQuery(id+"F0.wireOp",EDGE,"E5"),sQuery(id+"F0.wireOp",EDGE,"E6"),sQuery(id+"F0.wireOp",EDGE,"E7"),sQuery(id+"F0.wireOp",EDGE,"E8"),sQuery(id+"F0.wireOp",EDGE,"E9.left"),sQuery(id+"F0.wireOp",EDGE,"E9.right"),sQuery(id+"F0.wireOp",EDGE,"E10.bottom"),sQuery(id+"F0.wireOp",EDGE,"E10.top"),sQuery(id+"F0.wireOp",EDGE,"E11"),sQuery(id+"F0.wireOp",EDGE,"E12"),sQuery(id+"F0.wireOp",EDGE,"E13"),sQuery(id+"F0.wireOp",EDGE,"E14"),sQuery(id+"F0.wireOp",EDGE,"E15.0.1.0"),sQuery(id+"F0.wireOp",EDGE,"E15.0.1.1"),sQuery(id+"F0.wireOp",EDGE,"E15.0.1.2"),sQuery(id+"F0.wireOp",EDGE,"E15.0.1.3"),sQuery(id+"F0.wireOp",EDGE,"E15.0.2.0"),sQuery(id+"F0.wireOp",EDGE,"E15.0.2.1"),sQuery(id+"F0.wireOp",EDGE,"E15.0.2.2"),sQuery(id+"F0.wireOp",EDGE,"E15.0.2.3"),sQuery(id+"F0.wireOp",EDGE,"E16"),sQuery(id+"F0.wireOp",EDGE,"E17"),sQuery(id+"F0.wireOp",EDGE,"E18"),sQuery(id+"F0.wireOp",EDGE,"E19.left"),sQuery(id+"F0.wireOp",EDGE,"E20"),sQuery(id+"F0.wireOp",EDGE,"E21"),sQuery(id+"F0.wireOp",EDGE,"E22.left"),sQuery(id+"F0.wireOp",EDGE,"E23"),sQuery(id+"F0.wireOp",EDGE,"E24"),sQuery(id+"F0.wireOp",EDGE,"E25.1.0.0"),sQuery(id+"F0.wireOp",EDGE,"E25.1.0.1"),sQuery(id+"F0.wireOp",EDGE,"E25.1.0.2"),sQuery(id+"F0.wireOp",EDGE,"E27.MirrorCS"),sQuery(id+"F0.wireOp",EDGE,"E28.MirrorCS"),sQuery(id+"F0.wireOp",EDGE,"E29.MirrorCS"),sQuery(id+"F0.wireOp",EDGE,"E30.MirrorCS"),sQuery(id+"F0.wireOp",EDGE,"E31.MirrorCS"),sQuery(id+"F0.wireOp",EDGE,"E32.MirrorCS"),sQuery(id+"F0.wireOp",EDGE,"E33.MirrorCS"),sQuery(id+"F0.wireOp",EDGE,"E34.MirrorCS"),sQuery(id+"F0.wireOp",EDGE,"E35.MirrorCS"),sQuery(id+"F0.wireOp",EDGE,"E36.MirrorCS"),sQuery(id+"F0.wireOp",EDGE,"E37.MirrorCS"),sQuery(id+"F0.wireOp",EDGE,"E38.MirrorCS"),sQuery(id+"F0.wireOp",EDGE,"E39.MirrorCS"),sQuery(id+"F0.wireOp",EDGE,"E40.MirrorCS"),sQuery(id+"F0.wireOp",EDGE,"E41.MirrorCS"),sQuery(id+"F0.wireOp",EDGE,"E42.MirrorCS"),sQuery(id+"F0.wireOp",EDGE,"E43.MirrorCS"),sQuery(id+"F0.wireOp",EDGE,"E44.MirrorCS"),sQuery(id+"F0.wireOp",EDGE,"E45.MirrorCS"),sQuery(id+"F0.wireOp",EDGE,"E46.MirrorC"),sQuery(id+"F0.wireOp",EDGE,"E47.MirrorC"),sQuery(id+"F0.wireOp",EDGE,"E48.MirrorC"),sQuery(id+"F0.wireOp",EDGE,"E49.MirrorC"),sQuery(id+"F0.wireOp",EDGE,"E52.MirrorC"),sQuery(id+"F0.wireOp",EDGE,"E53.MirrorCS"),sQuery(id+"F0.wireOp",EDGE,"E54.MirrorCS"),sQuery(id+"F0.wireOp",EDGE,"E55.MirrorCS"),sQuery(id+"F0.wireOp",EDGE,"E58.MirrorCS"),sQuery(id+"F0.wireOp",EDGE,"E59.MirrorCS"),sQuery(id+"F0.wireOp",EDGE,"E60.MirrorCS"),sQuery(id+"F0.wireOp",EDGE,"E61.MirrorCS"),sQuery(id+"F0.wireOp",EDGE,"E62.MirrorCS"),sQuery(id+"F0.wireOp",EDGE,"E63.MirrorCS"),sQuery(id+"F0.wireOp",EDGE,"E64.MirrorCS"),sQuery(id+"F0.wireOp",EDGE,"E65.MirrorCS"),sQuery(id+"F0.wireOp",EDGE,"E66.MirrorCS"),sQuery(id+"F0.wireOp",EDGE,"E67"),sQuery(id+"F0.wireOp",EDGE,"E68"),sQuery(id+"F0.wireOp",EDGE,"E69"),sQuery(id+"F0.wireOp",EDGE,"E70.trimOffspring"),sQuery(id+"F0.wireOp",EDGE,"E71.filletArc"),sQuery(id+"F0.wireOp",EDGE,"E72.filletArc"),sQuery(id+"F0.wireOp",EDGE,"E73.filletArc"),sQuery(id+"F0.wireOp",EDGE,"E74.filletArc"),sQuery(id+"F0.wireOp",EDGE,"E75.MirrorCS"),sQuery(id+"F0.wireOp",EDGE,"E76.MirrorCS"),sQuery(id+"F0.wireOp",EDGE,"E77.MirrorCS"),sQuery(id+"F0.wireOp",EDGE,"E78.MirrorCS"),sQuery(id+"F0.wireOp",EDGE,"E79.MirrorCS"),sQuery(id+"F0.wireOp",EDGE,"E80.MirrorCS"),sQuery(id+"F0.wireOp",EDGE,"E81.MirrorCS"),sQuery(id+"F0.wireOp",EDGE,"E82.trimOffspring")])]});
            var Q1;
            Q1=qCreatedBy(makeId("Right.planeOp"),FACE);
            mirror(context, id + "F11", {"operationType" : NewBodyOperationType.ADD, "entities" : qUnion([Q0]), "mirrorPlane" : qUnion([Q1])});
        }
        {
            var Q0;
            Q0=makeQuery(id+"F8.opExtrude","CAP_EDGE",EDGE,{"disambiguationData":[OSD([sQuery(id+"F7.wireOp",EDGE,"E128")])],"isStart":false});
            var Q1;
            Q1=makeQuery(id+"F11.opPattern","COPY",EDGE,{"derivedFrom":makeQuery(id+"F8.opExtrude","CAP_EDGE",EDGE,{"disambiguationData":[OSD([sQuery(id+"F7.wireOp",EDGE,"E128")])],"isStart":false}),"instanceName":"1"});
            fillet(context, id + "F12", {"entities" : qUnion([Q0, Q1]), "radius" : 2 * mm, "tangentPropagation" : true, "allowEdgeOverflow" : false});
        }
        {
            var Q0;
            Q0=makeQuery(id+"F1.opExtrude","SWEPT_FACE",FACE,{"disambiguationData":[OSD([sQuery(id+"F0.wireOp",EDGE,"E2"),sQuery(id+"F0.wireOp",EDGE,"E65.MirrorCS")])]});
            var sketch = newSketch(context, id + "F13", { "sketchPlane" : qUnion([Q0])});
            skLineSegment(sketch, "E172", {"start": v(-34.75, 0) * mm, "end": v(-34.75, -5) * mm});
            skLineSegment(sketch, "E173", {"start": v(-34.75, -5) * mm, "end": v(-21.03, -37.55) * mm});
            skLineSegment(sketch, "E174", {"start": v(-20, -40) * mm, "end": v(0, -40) * mm, "construction": true});
            skLineSegment(sketch, "E175", {"start": v(-14, -40) * mm, "end": v(-14, -29) * mm});
            skArc(sketch, "E176", {"start": v(0, -15) * mm, "mid": v(-9.17, -18.42) * mm, "end": v(-13.86, -27) * mm});
            skPoint(sketch, "E177", {"position": v(-14, -29) * mm});
            skLineSegment(sketch, "E178", {"start": v(-14, -29) * mm, "end": v(0, -29) * mm, "construction": true});
            skLineSegment(sketch, "E179", {"start": v(0, -29) * mm, "end": v(0, -15) * mm, "construction": true});
            skLineSegment(sketch, "E180", {"start": v(-17.34, -40) * mm, "end": v(-14, -40) * mm});
            skLineSegment(sketch, "E181.MirrorCS", {"start": v(17.34, -40) * mm, "end": v(14, -40) * mm});
            skLineSegment(sketch, "E182.MirrorCS", {"start": v(14, -29) * mm, "end": v(0, -29) * mm, "construction": true});
            skArc(sketch, "E183.MirrorCS", {"start": v(0, -15) * mm, "mid": v(9.17, -18.42) * mm, "end": v(13.86, -27) * mm});
            skLineSegment(sketch, "E184.MirrorCS", {"start": v(14, -40) * mm, "end": v(14, -29) * mm});
            skLineSegment(sketch, "E185.MirrorCS", {"start": v(20, -40) * mm, "end": v(0, -40) * mm, "construction": true});
            skPoint(sketch, "E186.MirrorP", {"position": v(14, -29) * mm});
            skLineSegment(sketch, "E187.MirrorCS", {"start": v(34.75, 0) * mm, "end": v(34.75, -5) * mm});
            skLineSegment(sketch, "E188.MirrorCS", {"start": v(34.75, -5) * mm, "end": v(21.03, -37.55) * mm});
            skLineSegment(sketch, "E189", {"start": v(-34.75, 0) * mm, "end": v(34.75, 0) * mm});
            skArc(sketch, "E190", {"start": v(-16, -27) * mm, "mid": v(-17, -28) * mm, "end": v(-16, -29) * mm});
            skLineSegment(sketch, "E191", {"start": v(-16, -27) * mm, "end": v(-14, -27) * mm});
            skLineSegment(sketch, "E192", {"start": v(-16, -29) * mm, "end": v(-14, -29) * mm});
            skLineSegment(sketch, "E193", {"start": v(-14, -27) * mm, "end": v(-13.86, -27) * mm});
            skArc(sketch, "E194.MirrorCS", {"start": v(16, -27) * mm, "mid": v(17, -28) * mm, "end": v(16, -29) * mm});
            skLineSegment(sketch, "E195.MirrorCS", {"start": v(16, -29) * mm, "end": v(14, -29) * mm});
            skLineSegment(sketch, "E196.MirrorCS", {"start": v(16, -27) * mm, "end": v(14, -27) * mm});
            skLineSegment(sketch, "E197.MirrorCS", {"start": v(14, -27) * mm, "end": v(13.86, -27) * mm});
            skPoint(sketch, "E198.orphan", {"position": v(14, -27) * mm});
            skPoint(sketch, "E199.visualSharp", {"position": v(-20, -40) * mm});
            skArc(sketch, "E199.filletArc", {"start": v(-21.03, -37.55) * mm, "mid": v(-19.56, -39.33) * mm, "end": v(-17.34, -40) * mm});
            skPoint(sketch, "E200.visualSharp", {"position": v(20, -40) * mm});
            skArc(sketch, "E200.filletArc", {"start": v(17.34, -40) * mm, "mid": v(19.56, -39.33) * mm, "end": v(21.03, -37.55) * mm});
            skSolve(sketch);
        }
        {
            var Q0;
            Q0=qSketchRegion(id+"F13",true);
            extrude(context, id + "F14", {"entities" : qUnion([Q0]), "operationType" : NewBodyOperationType.ADD, "depth" : 1.5 * mm, "offsetDistance" : 25 * mm});
        }
        {
            var Q0;
            Q0=makeQuery(id+"F14.opExtrude","CAP_FACE",FACE,{"disambiguationData":[OSD([sQuery(id+"F13.wireOp",EDGE,"E172"),sQuery(id+"F13.wireOp",EDGE,"E173"),sQuery(id+"F13.wireOp",EDGE,"E175"),sQuery(id+"F13.wireOp",EDGE,"E176"),sQuery(id+"F13.wireOp",EDGE,"E180"),sQuery(id+"F13.wireOp",EDGE,"E181.MirrorCS"),sQuery(id+"F13.wireOp",EDGE,"E183.MirrorCS"),sQuery(id+"F13.wireOp",EDGE,"E184.MirrorCS"),sQuery(id+"F13.wireOp",EDGE,"E187.MirrorCS"),sQuery(id+"F13.wireOp",EDGE,"E188.MirrorCS"),sQuery(id+"F13.wireOp",EDGE,"E189"),sQuery(id+"F13.wireOp",EDGE,"E190"),sQuery(id+"F13.wireOp",EDGE,"E191"),sQuery(id+"F13.wireOp",EDGE,"E192"),sQuery(id+"F13.wireOp",EDGE,"E193"),sQuery(id+"F13.wireOp",EDGE,"E194.MirrorCS"),sQuery(id+"F13.wireOp",EDGE,"E195.MirrorCS"),sQuery(id+"F13.wireOp",EDGE,"E196.MirrorCS"),sQuery(id+"F13.wireOp",EDGE,"E197.MirrorCS"),sQuery(id+"F13.wireOp",EDGE,"E199.filletArc"),sQuery(id+"F13.wireOp",EDGE,"E200.filletArc")])],"isStart":false});
            var sketch = newSketch(context, id + "F15", { "sketchPlane" : qUnion([Q0])});
            skArc(sketch, "E201", {"start": v(-26.22, -8) * mm, "mid": v(-27.75, -9.52) * mm, "end": v(-26.22, -11.05) * mm});
            skLineSegment(sketch, "E202", {"start": v(-26.22, -8) * mm, "end": v(-18.25, -8) * mm});
            skLineSegment(sketch, "E203", {"start": v(-26.22, -11.05) * mm, "end": v(-18.25, -11.05) * mm});
            skLineSegment(sketch, "E204", {"start": v(-18.25, -8) * mm, "end": v(-18.25, -11.05) * mm, "construction": true});
            skLineSegment(sketch, "E205.MirrorCS", {"start": v(-10.27, -8) * mm, "end": v(-18.25, -8) * mm});
            skLineSegment(sketch, "E206.MirrorCS", {"start": v(-10.27, -11.05) * mm, "end": v(-18.25, -11.05) * mm});
            skArc(sketch, "E207.MirrorCS", {"start": v(-10.27, -8) * mm, "mid": v(-8.75, -9.52) * mm, "end": v(-10.27, -11.05) * mm});
            skLineSegment(sketch, "E208", {"start": v(-26.22, -9.52) * mm, "end": v(-26.22, -8) * mm, "construction": true});
            skLineSegment(sketch, "E209", {"start": v(-23.22, -16.02) * mm, "end": v(-17.22, -16.02) * mm});
            skArc(sketch, "E210.0.startCap", {"start": v(-23.22, -17.52) * mm, "mid": v(-24.72, -16.02) * mm, "end": v(-23.22, -14.52) * mm});
            skArc(sketch, "E210.0.endCap", {"start": v(-17.22, -14.52) * mm, "mid": v(-15.72, -16.02) * mm, "end": v(-17.22, -17.52) * mm});
            skLineSegment(sketch, "E210.0.left", {"start": v(-23.22, -14.52) * mm, "end": v(-17.22, -14.52) * mm});
            skLineSegment(sketch, "E210.0.right", {"start": v(-23.22, -17.52) * mm, "end": v(-17.22, -17.52) * mm});
            skLineSegment(sketch, "E211.MirrorCS", {"start": v(23.22, -17.52) * mm, "end": v(17.22, -17.52) * mm});
            skLineSegment(sketch, "E212.MirrorCS", {"start": v(23.22, -14.52) * mm, "end": v(17.22, -14.52) * mm});
            skArc(sketch, "E213.MirrorCS", {"start": v(17.22, -14.52) * mm, "mid": v(15.72, -16.02) * mm, "end": v(17.22, -17.52) * mm});
            skArc(sketch, "E214.MirrorCS", {"start": v(23.22, -17.52) * mm, "mid": v(24.72, -16.02) * mm, "end": v(23.22, -14.52) * mm});
            skLineSegment(sketch, "E215.MirrorCS", {"start": v(26.22, -11.05) * mm, "end": v(18.25, -11.05) * mm});
            skLineSegment(sketch, "E216.MirrorCS", {"start": v(10.27, -8) * mm, "end": v(18.25, -8) * mm});
            skLineSegment(sketch, "E217.MirrorCS", {"start": v(10.27, -11.05) * mm, "end": v(18.25, -11.05) * mm});
            skLineSegment(sketch, "E218.MirrorCS", {"start": v(26.22, -9.52) * mm, "end": v(26.22, -8) * mm, "construction": true});
            skLineSegment(sketch, "E219.MirrorCS", {"start": v(18.25, -8) * mm, "end": v(18.25, -11.05) * mm, "construction": true});
            skArc(sketch, "E220.MirrorCS", {"start": v(10.27, -8) * mm, "mid": v(8.75, -9.52) * mm, "end": v(10.27, -11.05) * mm});
            skLineSegment(sketch, "E221.MirrorCS", {"start": v(23.22, -16.02) * mm, "end": v(17.22, -16.02) * mm});
            skLineSegment(sketch, "E222.MirrorCS", {"start": v(26.22, -8) * mm, "end": v(18.25, -8) * mm});
            skArc(sketch, "E223.MirrorCS", {"start": v(26.22, -8) * mm, "mid": v(27.75, -9.52) * mm, "end": v(26.22, -11.05) * mm});
            skSolve(sketch);
        }
        {
            var Q0;
            Q0=qSketchRegion(id+"F15",true);
            extrude(context, id + "F16", {"entities" : qUnion([Q0]), "operationType" : NewBodyOperationType.REMOVE, "oppositeDirection" : true, "depth" : 25 * mm, "offsetDistance" : 25 * mm});
        }
        {
            var Q0;
            Q0=makeQuery(id+"F14.opExtrude","SWEPT_FACE",FACE,{"disambiguationData":[OSD([sQuery(id+"F13.wireOp",EDGE,"E175")])]});
            var sketch = newSketch(context, id + "F17", { "sketchPlane" : qUnion([Q0])});
            skLineSegment(sketch, "E224", {"start": v(-67.99, -29) * mm, "end": v(-73.81, -36.46) * mm});
            skLineSegment(sketch, "E225", {"start": v(-71.09, -40) * mm, "end": v(-66.49, -40) * mm});
            skLineSegment(sketch, "E226", {"start": v(-66.49, -40) * mm, "end": v(-66.49, -29) * mm});
            skLineSegment(sketch, "E227", {"start": v(-66.49, -29) * mm, "end": v(-67.99, -29) * mm});
            skCircle(sketch, "E228", {"center": v(-70.99, -37) * mm, "radius": 0.93 * mm});
            skLineSegment(sketch, "E229", {"start": v(-74.24, -37.69) * mm, "end": v(-74.24, -38) * mm});
            skLineSegment(sketch, "E230", {"start": v(-72.24, -40) * mm, "end": v(-71.09, -40) * mm});
            skPoint(sketch, "E231.visualSharp", {"position": v(-74.24, -37) * mm});
            skArc(sketch, "E231.filletArc", {"start": v(-73.81, -36.46) * mm, "mid": v(-74.13, -37.04) * mm, "end": v(-74.24, -37.69) * mm});
            skPoint(sketch, "E232.visualSharp", {"position": v(-74.24, -40) * mm});
            skArc(sketch, "E232.filletArc", {"start": v(-74.24, -38) * mm, "mid": v(-73.65, -39.41) * mm, "end": v(-72.24, -40) * mm});
            skSolve(sketch);
        }
        {
            var Q0;
            Q0=qSketchRegion(id+"F17",true);
            extrude(context, id + "F18", {"entities" : qUnion([Q0]), "operationType" : NewBodyOperationType.ADD, "oppositeDirection" : true, "depth" : 1.5 * mm, "offsetDistance" : 25 * mm});
        }
        {
            var Q0;
            Q0=makeQuery(id+"F1.opExtrude","SWEPT_BODY",BODY,{"disambiguationData":[OSD([sQuery(id+"F0.wireOp",EDGE,"E0"),sQuery(id+"F0.wireOp",EDGE,"E1"),sQuery(id+"F0.wireOp",EDGE,"E2"),sQuery(id+"F0.wireOp",EDGE,"E4"),sQuery(id+"F0.wireOp",EDGE,"E5"),sQuery(id+"F0.wireOp",EDGE,"E6"),sQuery(id+"F0.wireOp",EDGE,"E7"),sQuery(id+"F0.wireOp",EDGE,"E8"),sQuery(id+"F0.wireOp",EDGE,"E9.left"),sQuery(id+"F0.wireOp",EDGE,"E9.right"),sQuery(id+"F0.wireOp",EDGE,"E10.bottom"),sQuery(id+"F0.wireOp",EDGE,"E10.top"),sQuery(id+"F0.wireOp",EDGE,"E11"),sQuery(id+"F0.wireOp",EDGE,"E12"),sQuery(id+"F0.wireOp",EDGE,"E13"),sQuery(id+"F0.wireOp",EDGE,"E14"),sQuery(id+"F0.wireOp",EDGE,"E15.0.1.0"),sQuery(id+"F0.wireOp",EDGE,"E15.0.1.1"),sQuery(id+"F0.wireOp",EDGE,"E15.0.1.2"),sQuery(id+"F0.wireOp",EDGE,"E15.0.1.3"),sQuery(id+"F0.wireOp",EDGE,"E15.0.2.0"),sQuery(id+"F0.wireOp",EDGE,"E15.0.2.1"),sQuery(id+"F0.wireOp",EDGE,"E15.0.2.2"),sQuery(id+"F0.wireOp",EDGE,"E15.0.2.3"),sQuery(id+"F0.wireOp",EDGE,"E16"),sQuery(id+"F0.wireOp",EDGE,"E17"),sQuery(id+"F0.wireOp",EDGE,"E18"),sQuery(id+"F0.wireOp",EDGE,"E19.left"),sQuery(id+"F0.wireOp",EDGE,"E20"),sQuery(id+"F0.wireOp",EDGE,"E21"),sQuery(id+"F0.wireOp",EDGE,"E22.left"),sQuery(id+"F0.wireOp",EDGE,"E23"),sQuery(id+"F0.wireOp",EDGE,"E24"),sQuery(id+"F0.wireOp",EDGE,"E25.1.0.0"),sQuery(id+"F0.wireOp",EDGE,"E25.1.0.1"),sQuery(id+"F0.wireOp",EDGE,"E25.1.0.2"),sQuery(id+"F0.wireOp",EDGE,"E27.MirrorCS"),sQuery(id+"F0.wireOp",EDGE,"E28.MirrorCS"),sQuery(id+"F0.wireOp",EDGE,"E29.MirrorCS"),sQuery(id+"F0.wireOp",EDGE,"E30.MirrorCS"),sQuery(id+"F0.wireOp",EDGE,"E31.MirrorCS"),sQuery(id+"F0.wireOp",EDGE,"E32.MirrorCS"),sQuery(id+"F0.wireOp",EDGE,"E33.MirrorCS"),sQuery(id+"F0.wireOp",EDGE,"E34.MirrorCS"),sQuery(id+"F0.wireOp",EDGE,"E35.MirrorCS"),sQuery(id+"F0.wireOp",EDGE,"E36.MirrorCS"),sQuery(id+"F0.wireOp",EDGE,"E37.MirrorCS"),sQuery(id+"F0.wireOp",EDGE,"E38.MirrorCS"),sQuery(id+"F0.wireOp",EDGE,"E39.MirrorCS"),sQuery(id+"F0.wireOp",EDGE,"E40.MirrorCS"),sQuery(id+"F0.wireOp",EDGE,"E41.MirrorCS"),sQuery(id+"F0.wireOp",EDGE,"E42.MirrorCS"),sQuery(id+"F0.wireOp",EDGE,"E43.MirrorCS"),sQuery(id+"F0.wireOp",EDGE,"E44.MirrorCS"),sQuery(id+"F0.wireOp",EDGE,"E45.MirrorCS"),sQuery(id+"F0.wireOp",EDGE,"E46.MirrorC"),sQuery(id+"F0.wireOp",EDGE,"E47.MirrorC"),sQuery(id+"F0.wireOp",EDGE,"E48.MirrorC"),sQuery(id+"F0.wireOp",EDGE,"E49.MirrorC"),sQuery(id+"F0.wireOp",EDGE,"E52.MirrorC"),sQuery(id+"F0.wireOp",EDGE,"E53.MirrorCS"),sQuery(id+"F0.wireOp",EDGE,"E54.MirrorCS"),sQuery(id+"F0.wireOp",EDGE,"E55.MirrorCS"),sQuery(id+"F0.wireOp",EDGE,"E58.MirrorCS"),sQuery(id+"F0.wireOp",EDGE,"E59.MirrorCS"),sQuery(id+"F0.wireOp",EDGE,"E60.MirrorCS"),sQuery(id+"F0.wireOp",EDGE,"E61.MirrorCS"),sQuery(id+"F0.wireOp",EDGE,"E62.MirrorCS"),sQuery(id+"F0.wireOp",EDGE,"E63.MirrorCS"),sQuery(id+"F0.wireOp",EDGE,"E64.MirrorCS"),sQuery(id+"F0.wireOp",EDGE,"E65.MirrorCS"),sQuery(id+"F0.wireOp",EDGE,"E66.MirrorCS"),sQuery(id+"F0.wireOp",EDGE,"E67"),sQuery(id+"F0.wireOp",EDGE,"E68"),sQuery(id+"F0.wireOp",EDGE,"E69"),sQuery(id+"F0.wireOp",EDGE,"E70.trimOffspring"),sQuery(id+"F0.wireOp",EDGE,"E71.filletArc"),sQuery(id+"F0.wireOp",EDGE,"E72.filletArc"),sQuery(id+"F0.wireOp",EDGE,"E73.filletArc"),sQuery(id+"F0.wireOp",EDGE,"E74.filletArc"),sQuery(id+"F0.wireOp",EDGE,"E75.MirrorCS"),sQuery(id+"F0.wireOp",EDGE,"E76.MirrorCS"),sQuery(id+"F0.wireOp",EDGE,"E77.MirrorCS"),sQuery(id+"F0.wireOp",EDGE,"E78.MirrorCS"),sQuery(id+"F0.wireOp",EDGE,"E79.MirrorCS"),sQuery(id+"F0.wireOp",EDGE,"E80.MirrorCS"),sQuery(id+"F0.wireOp",EDGE,"E81.MirrorCS"),sQuery(id+"F0.wireOp",EDGE,"E82.trimOffspring")])]});
            var Q1;
            Q1=qCreatedBy(makeId("Right.planeOp"),FACE);
            mirror(context, id + "F19", {"operationType" : NewBodyOperationType.ADD, "entities" : qUnion([Q0]), "mirrorPlane" : qUnion([Q1])});
        }
    });
